# Revit family: Accessory-Cabinet_Knob-KOHLER-HELST-K-33529
name_source: partatom
category: Specialty Equipment
revit_build: Autodesk Revit 2017 (Build: 20160225_1515(x64)
units: mm (PartAtom-declared; Revit-internal decimal feet)

## family parameters
Cut with Voids When Loaded = No
Host = Face
OmniClass Number = 23.31.25.00
OmniClass Title = Toilet and Bath Specialties
Part Type = Normal
Room Calculation Point = No
Round Connector Dimension = Use Diameter
Shared = No

## types (4) — shared parameters
ADA Compliant = No
Assembly Code = E20
Date Modified = 02/19/2021
Default Elevation = 0"
Description = CABINET KNOB 1 INCHES
Height = 7/8"
Length = 15/16"
Manufacturer = KOHLER Co.
Master Format 2014 = 06 41 93
Master Format 2014 Name = Cabinet and Drawer Hardware
Material = Zinc
Product Documentation Link = https://www.us.kohler.com
Product Name = HELST
Product Page URL = http://www.us.kohler.com
URL = https://www.us.kohler.com
WaterSense Certified = No
Width = 7/8"

## per-type parameters (varying)
| type | Finish | Model | Type |
| HF1-Polished Chrome | KOHLER-Metal-HF1-Chrome | K-33529-HF1 | 1 |
| HF3-Matte Black | KOHLER-Metal-HF3-Black | K-33529-HF3 | 2 |
| HF4-Brushed Nickel | KOHLER-Metal-HF4-Brushed_Nickel | K-33529-HF4 | 3 |
| HF6-Modern Brushed Brass | KOHLER-Metal-HF6-Modern_Brushed_Brass | K-33529-HF6 | 4 |

## geometry (parser evidence)
native form markers: Sweep x5
no freeform markers — native parametric forms only
